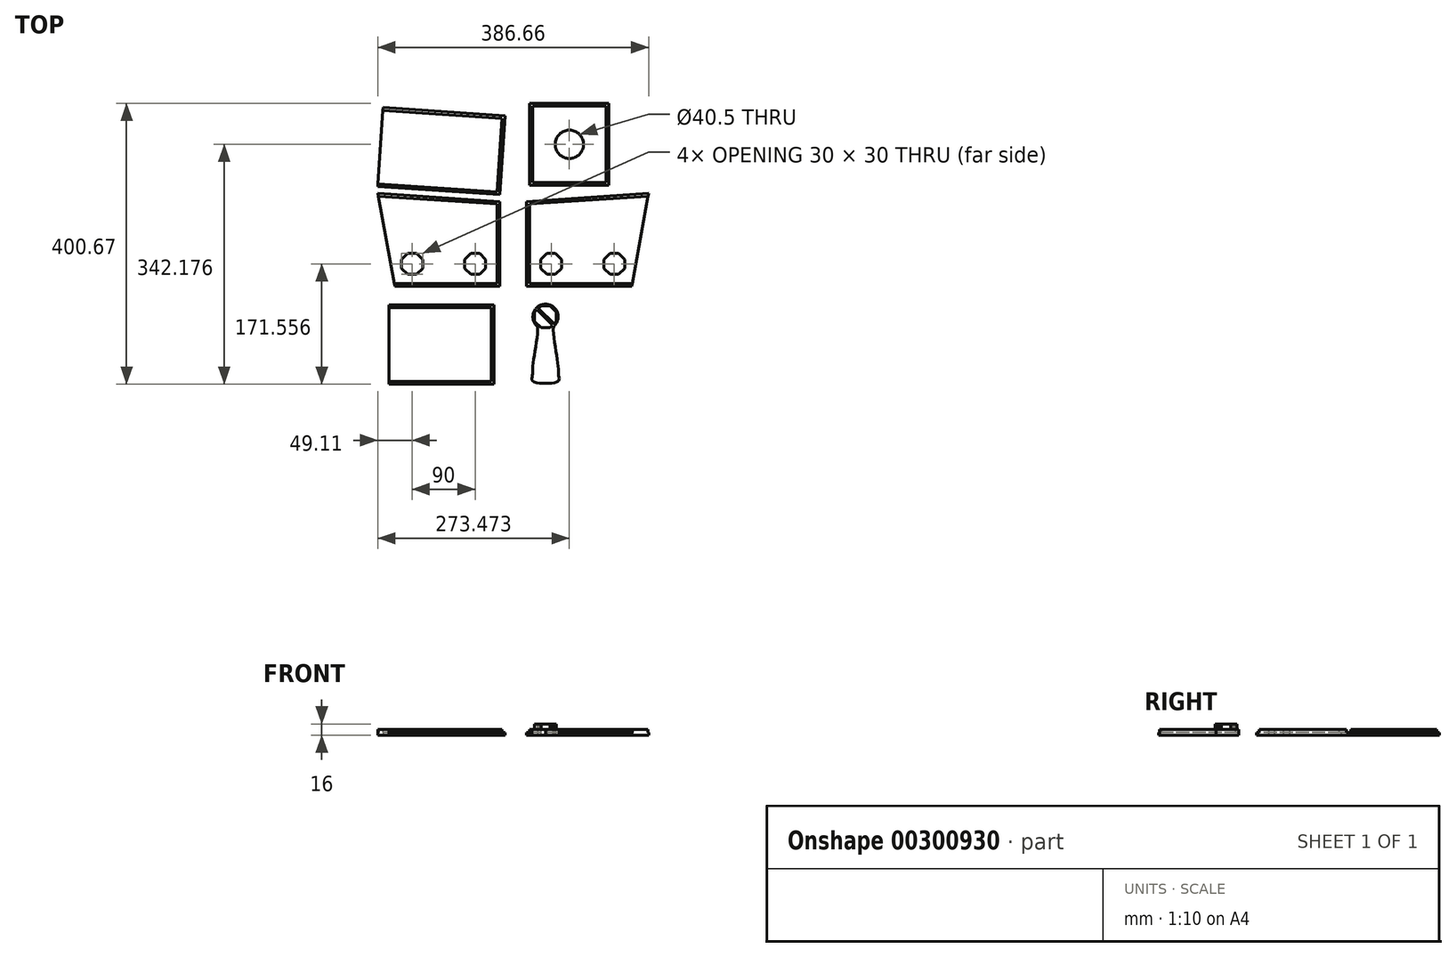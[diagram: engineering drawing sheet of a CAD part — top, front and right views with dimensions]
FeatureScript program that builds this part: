
annotation { "Feature Type Name" : "Feature", "Feature Type Description" : "" }
export const myFeature = defineFeature(function(context is Context, id is Id, definition is map)
    precondition{}
    {
        {
            assignVariable(context, id + "F0", {"name" : "mthick", "anyValue" : 8});
        }
        {
            var Q0;
            Q0=qCreatedBy(makeId("Top.planeOp"),FACE);
            var sketch = newSketch(context, id + "F1", { "sketchPlane" : qUnion([Q0])});
            skLineSegment(sketch, "E0", {"start": v(-19.22, -95.95) * mm, "end": v(-169.22, -95.95) * mm});
            skLineSegment(sketch, "E1", {"start": v(-169.22, -95.95) * mm, "end": v(-193.33, 36.65) * mm});
            skLineSegment(sketch, "E2", {"start": v(-193.33, 36.65) * mm, "end": v(-19.22, 25.05) * mm});
            skLineSegment(sketch, "E3", {"start": v(-19.22, 25.05) * mm, "end": v(-19.22, -95.95) * mm});
            skLineSegment(sketch, "E4", {"start": v(-169.22, -95.95) * mm, "end": v(-169.22, 35.05) * mm, "construction": true});
            skLineSegment(sketch, "E5", {"start": v(-19.22, 25.05) * mm, "end": v(-191.22, 25.05) * mm, "construction": true});
            skLineSegment(sketch, "E6", {"start": v(-60.43, -78.95) * mm, "end": v(-48, -78.95) * mm});
            skLineSegment(sketch, "E7", {"start": v(-48, -78.95) * mm, "end": v(-39.22, -70.17) * mm});
            skLineSegment(sketch, "E8", {"start": v(-39.22, -70.17) * mm, "end": v(-39.22, -57.74) * mm});
            skLineSegment(sketch, "E9", {"start": v(-39.22, -57.74) * mm, "end": v(-48, -48.95) * mm});
            skLineSegment(sketch, "E10", {"start": v(-48, -48.95) * mm, "end": v(-60.43, -48.95) * mm});
            skLineSegment(sketch, "E11", {"start": v(-60.43, -48.95) * mm, "end": v(-69.22, -57.74) * mm});
            skLineSegment(sketch, "E12", {"start": v(-69.22, -57.74) * mm, "end": v(-69.22, -70.17) * mm});
            skLineSegment(sketch, "E13", {"start": v(-69.22, -70.17) * mm, "end": v(-60.43, -78.95) * mm});
            skLineSegment(sketch, "E14", {"start": v(-60.43, -78.95) * mm, "end": v(-60.43, -48.95) * mm, "construction": true});
            skLineSegment(sketch, "E15", {"start": v(-69.22, -57.74) * mm, "end": v(-39.22, -57.74) * mm, "construction": true});
            skLineSegment(sketch, "E16.1.0.0", {"start": v(-129.22, -57.74) * mm, "end": v(-138, -48.95) * mm});
            skLineSegment(sketch, "E16.1.0.1", {"start": v(-150.43, -78.95) * mm, "end": v(-138, -78.95) * mm});
            skLineSegment(sketch, "E16.1.0.2", {"start": v(-138, -78.95) * mm, "end": v(-129.22, -70.17) * mm});
            skLineSegment(sketch, "E16.1.0.3", {"start": v(-159.22, -57.74) * mm, "end": v(-129.22, -57.74) * mm, "construction": true});
            skLineSegment(sketch, "E16.1.0.4", {"start": v(-159.22, -57.74) * mm, "end": v(-159.22, -70.17) * mm});
            skLineSegment(sketch, "E16.1.0.5", {"start": v(-150.43, -78.95) * mm, "end": v(-150.43, -48.95) * mm, "construction": true});
            skLineSegment(sketch, "E16.1.0.6", {"start": v(-150.43, -48.95) * mm, "end": v(-159.22, -57.74) * mm});
            skLineSegment(sketch, "E16.1.0.7", {"start": v(-138, -48.95) * mm, "end": v(-150.43, -48.95) * mm});
            skLineSegment(sketch, "E16.1.0.8", {"start": v(-129.22, -70.17) * mm, "end": v(-129.22, -57.74) * mm});
            skLineSegment(sketch, "E16.1.0.9", {"start": v(-159.22, -70.17) * mm, "end": v(-150.43, -78.95) * mm});
            skLineSegment(sketch, "E16.direction1", {"start": v(-69.22, -57.74) * mm, "end": v(-159.22, -57.74) * mm, "construction": true});
            skLineSegment(sketch, "E17.0", {"start": v(-23.22, -91.95) * mm, "end": v(-169.95, -91.95) * mm});
            skLineSegment(sketch, "E17.1", {"start": v(-23.22, 21.3) * mm, "end": v(-23.22, -91.95) * mm});
            skLineSegment(sketch, "E17.2", {"start": v(-192.6, 32.6) * mm, "end": v(-23.22, 21.3) * mm});
            skLineSegment(sketch, "E18.MirrorCS", {"start": v(60.43, -48.95) * mm, "end": v(69.22, -57.74) * mm});
            skLineSegment(sketch, "E19.MirrorCS", {"start": v(150.43, -48.95) * mm, "end": v(159.22, -57.74) * mm});
            skLineSegment(sketch, "E20.MirrorCS", {"start": v(69.22, -70.17) * mm, "end": v(60.43, -78.95) * mm});
            skLineSegment(sketch, "E21.MirrorCS", {"start": v(48, -48.95) * mm, "end": v(60.43, -48.95) * mm});
            skLineSegment(sketch, "E22.MirrorCS", {"start": v(138, -48.95) * mm, "end": v(150.43, -48.95) * mm});
            skLineSegment(sketch, "E23.MirrorCS", {"start": v(39.22, -57.74) * mm, "end": v(48, -48.95) * mm});
            skLineSegment(sketch, "E24.MirrorCS", {"start": v(129.22, -70.17) * mm, "end": v(129.22, -57.74) * mm});
            skLineSegment(sketch, "E25.MirrorCS", {"start": v(159.22, -57.74) * mm, "end": v(159.22, -70.17) * mm});
            skLineSegment(sketch, "E26.MirrorCS", {"start": v(129.22, -57.74) * mm, "end": v(138, -48.95) * mm});
            skLineSegment(sketch, "E27.MirrorCS", {"start": v(159.22, -70.17) * mm, "end": v(150.43, -78.95) * mm});
            skLineSegment(sketch, "E28.MirrorCS", {"start": v(69.22, -57.74) * mm, "end": v(69.22, -70.17) * mm});
            skLineSegment(sketch, "E29.MirrorCS", {"start": v(39.22, -70.17) * mm, "end": v(39.22, -57.74) * mm});
            skLineSegment(sketch, "E30.MirrorCS", {"start": v(150.43, -78.95) * mm, "end": v(138, -78.95) * mm});
            skLineSegment(sketch, "E31.MirrorCS", {"start": v(60.43, -78.95) * mm, "end": v(48, -78.95) * mm});
            skLineSegment(sketch, "E32.MirrorCS", {"start": v(138, -78.95) * mm, "end": v(129.22, -70.17) * mm});
            skLineSegment(sketch, "E33.MirrorCS", {"start": v(48, -78.95) * mm, "end": v(39.22, -70.17) * mm});
            skLineSegment(sketch, "E34.MirrorCS", {"start": v(150.43, -78.95) * mm, "end": v(150.43, -48.95) * mm, "construction": true});
            skLineSegment(sketch, "E35.MirrorCS", {"start": v(23.22, -91.95) * mm, "end": v(169.95, -91.95) * mm});
            skLineSegment(sketch, "E36.MirrorCS", {"start": v(192.6, 32.6) * mm, "end": v(23.22, 21.3) * mm});
            skLineSegment(sketch, "E37.MirrorCS", {"start": v(23.22, 21.3) * mm, "end": v(23.22, -91.95) * mm});
            skLineSegment(sketch, "E38.MirrorCS", {"start": v(169.22, -95.95) * mm, "end": v(193.33, 36.65) * mm});
            skLineSegment(sketch, "E39.MirrorCS", {"start": v(69.22, -57.74) * mm, "end": v(39.22, -57.74) * mm, "construction": true});
            skLineSegment(sketch, "E40.MirrorCS", {"start": v(19.22, -95.95) * mm, "end": v(169.22, -95.95) * mm});
            skLineSegment(sketch, "E41.MirrorCS", {"start": v(60.43, -78.95) * mm, "end": v(60.43, -48.95) * mm, "construction": true});
            skLineSegment(sketch, "E42.MirrorCS", {"start": v(193.33, 36.65) * mm, "end": v(19.22, 25.05) * mm});
            skLineSegment(sketch, "E43.MirrorCS", {"start": v(169.22, -95.95) * mm, "end": v(169.22, 35.05) * mm, "construction": true});
            skLineSegment(sketch, "E44.MirrorCS", {"start": v(19.22, 25.05) * mm, "end": v(191.22, 25.05) * mm, "construction": true});
            skLineSegment(sketch, "E45.MirrorCS", {"start": v(159.22, -57.74) * mm, "end": v(129.22, -57.74) * mm, "construction": true});
            skLineSegment(sketch, "E46.MirrorCS", {"start": v(69.22, -57.74) * mm, "end": v(159.22, -57.74) * mm, "construction": true});
            skLineSegment(sketch, "E47.MirrorCS", {"start": v(19.22, 25.05) * mm, "end": v(19.22, -95.95) * mm});
            skSolve(sketch);
        }
        {
            var Q0;
            Q0=qCreatedBy(makeId("Top.planeOp"),FACE);
            var sketch = newSketch(context, id + "F2", { "sketchPlane" : qUnion([Q0])});
            skLineSegment(sketch, "E48.bottom", {"start": v(-177.55, -122.5) * mm, "end": v(-27.55, -122.5) * mm});
            skLineSegment(sketch, "E48.top", {"start": v(-177.55, -235.5) * mm, "end": v(-27.55, -235.5) * mm});
            skLineSegment(sketch, "E48.left", {"start": v(-177.55, -122.5) * mm, "end": v(-177.55, -235.5) * mm});
            skLineSegment(sketch, "E48.right", {"start": v(-27.55, -122.5) * mm, "end": v(-27.55, -235.5) * mm});
            skLineSegment(sketch, "E49.0", {"start": v(-177.55, -231.5) * mm, "end": v(-31.55, -231.5) * mm});
            skLineSegment(sketch, "E49.1", {"start": v(-31.55, -126.5) * mm, "end": v(-31.55, -231.5) * mm});
            skLineSegment(sketch, "E49.2", {"start": v(-177.55, -126.5) * mm, "end": v(-31.55, -126.5) * mm});
            skSolve(sketch);
        }
        {
            var Q0;
            Q0=qCreatedBy(makeId("Top.planeOp"),FACE);
            var sketch = newSketch(context, id + "F3", { "sketchPlane" : qUnion([Q0])});
            skLineSegment(sketch, "E50.0", {"start": v(-193.33, 36.65) * mm, "end": v(-19.22, 25.05) * mm, "construction": true});
            skLineSegment(sketch, "E51", {"start": v(-193.33, 46.39) * mm, "end": v(-18.95, 34.76) * mm});
            skLineSegment(sketch, "E52", {"start": v(-18.95, 34.76) * mm, "end": v(-11.44, 147.51) * mm});
            skLineSegment(sketch, "E53", {"start": v(-11.44, 147.51) * mm, "end": v(-185.81, 159.14) * mm});
            skLineSegment(sketch, "E54", {"start": v(-185.81, 159.14) * mm, "end": v(-193.33, 46.39) * mm});
            skLineSegment(sketch, "E55.0", {"start": v(-15.7, 143.79) * mm, "end": v(-186.08, 155.15) * mm});
            skLineSegment(sketch, "E55.1", {"start": v(-22.68, 39.02) * mm, "end": v(-15.7, 143.79) * mm});
            skLineSegment(sketch, "E55.2", {"start": v(-193.06, 50.38) * mm, "end": v(-22.68, 39.02) * mm});
            skLineSegment(sketch, "E56.0", {"start": v(-192.6, 32.6) * mm, "end": v(-23.22, 21.3) * mm, "construction": true});
            skLineSegment(sketch, "E57.0", {"start": v(-19.22, 25.05) * mm, "end": v(-19.22, -95.95) * mm, "construction": true});
            skLineSegment(sketch, "E58", {"start": v(-23.22, 21.3) * mm, "end": v(-19.22, 21.04) * mm, "construction": true});
            skLineSegment(sketch, "E59", {"start": v(-19.22, 21.04) * mm, "end": v(-18.75, 28.14) * mm, "construction": true});
            skLineSegment(sketch, "E60", {"start": v(-19.22, 25.05) * mm, "end": v(-18.95, 25.03) * mm, "construction": true});
            skLineSegment(sketch, "E61", {"start": v(-193.33, 36.65) * mm, "end": v(-18.95, 25.03) * mm, "construction": true});
            skSolve(sketch);
        }
        {
            var Q0;
            Q0=qCreatedBy(makeId("Top.planeOp"),FACE);
            var sketch = newSketch(context, id + "F4", { "sketchPlane" : qUnion([Q0])});
            skPoint(sketch, "E62.0", {"position": v(-19.22, -95.95) * mm});
            skPoint(sketch, "E62.1", {"position": v(-19.22, 21.04) * mm});
            skLineSegment(sketch, "E63", {"start": v(-19.22, 21.04) * mm, "end": v(-19.22, -95.95) * mm, "construction": true});
            skLineSegment(sketch, "E64.bottom", {"start": v(136.64, 48.17) * mm, "end": v(23.64, 48.17) * mm});
            skLineSegment(sketch, "E64.top", {"start": v(136.64, 165.16) * mm, "end": v(23.64, 165.16) * mm});
            skLineSegment(sketch, "E64.left", {"start": v(136.64, 48.17) * mm, "end": v(136.64, 165.16) * mm});
            skLineSegment(sketch, "E64.right", {"start": v(23.64, 48.17) * mm, "end": v(23.64, 165.16) * mm});
            skPoint(sketch, "E64.middle", {"position": v(80.14, 106.67) * mm});
            skCircle(sketch, "E65", {"center": v(80.14, 106.67) * mm, "radius": 20.25 * mm});
            skLineSegment(sketch, "E66.0", {"start": v(132.64, 161.16) * mm, "end": v(27.64, 161.16) * mm});
            skLineSegment(sketch, "E66.1", {"start": v(132.64, 52.17) * mm, "end": v(132.64, 161.16) * mm});
            skLineSegment(sketch, "E66.2", {"start": v(132.64, 52.17) * mm, "end": v(27.64, 52.17) * mm});
            skLineSegment(sketch, "E66.3", {"start": v(27.64, 52.17) * mm, "end": v(27.64, 161.16) * mm});
            skSolve(sketch);
        }
        {
            var Q0;
            Q0=qCreatedBy(makeId("Top.planeOp"),FACE);
            var sketch = newSketch(context, id + "F5", { "sketchPlane" : qUnion([Q0])});
            skCircle(sketch, "E67", {"center": v(46.1, -139.4) * mm, "radius": 18 * mm});
            skLineSegment(sketch, "E68", {"start": v(46.1, -139.4) * mm, "end": v(46.1, -153.4) * mm, "construction": true});
            skLineSegment(sketch, "E69", {"start": v(46.1, -153.4) * mm, "end": v(34.78, -153.4) * mm, "construction": true});
            skLineSegment(sketch, "E70", {"start": v(46.1, -153.4) * mm, "end": v(57.4, -153.4) * mm, "construction": true});
            skLineSegment(sketch, "E71", {"start": v(46.1, -153.4) * mm, "end": v(46.1, -224.4) * mm, "construction": true});
            skLineSegment(sketch, "E72", {"start": v(46.1, -224.4) * mm, "end": v(27.1, -224.4) * mm, "construction": true});
            skLineSegment(sketch, "E73", {"start": v(46.1, -224.4) * mm, "end": v(46.1, -234.4) * mm, "construction": true});
            skFitSpline(sketch, "E74", {"points": [v(34.78, -153.4) * mm, v(28.54, -205.56) * mm, v(27.1, -224.4) * mm, v(27.1, -230.18) * mm, v(46.1, -234.4) * mm], "startDerivative": vector(7.27, -104.43) * mm, "endDerivative": vector(108.23, 10.07) * mm});
            skFitSpline(sketch, "E75.MirrorCS", {"points": [v(57.4, -153.4) * mm, v(63.64, -205.56) * mm, v(65.1, -224.4) * mm, v(65.1, -230.18) * mm, v(46.1, -234.4) * mm], "startDerivative": vector(-7.27, -104.43) * mm, "endDerivative": vector(-108.23, 10.07) * mm});
            skCircle(sketch, "E76.cCircle", {"center": v(46.1, -139.4) * mm, "radius": 15.5 * mm, "construction": true});
            skLineSegment(sketch, "E76.0", {"start": v(52.51, -123.9) * mm, "end": v(61.6, -132.98) * mm});
            skLineSegment(sketch, "E76.1", {"start": v(61.6, -132.98) * mm, "end": v(61.6, -145.82) * mm});
            skLineSegment(sketch, "E76.2", {"start": v(61.6, -145.82) * mm, "end": v(52.51, -154.9) * mm});
            skLineSegment(sketch, "E76.3", {"start": v(52.51, -154.9) * mm, "end": v(39.67, -154.9) * mm});
            skLineSegment(sketch, "E76.4", {"start": v(39.67, -154.9) * mm, "end": v(30.6, -145.82) * mm});
            skLineSegment(sketch, "E76.5", {"start": v(30.6, -145.82) * mm, "end": v(30.6, -132.98) * mm});
            skLineSegment(sketch, "E76.6", {"start": v(30.6, -132.98) * mm, "end": v(39.67, -123.9) * mm});
            skLineSegment(sketch, "E76.7", {"start": v(39.67, -123.9) * mm, "end": v(52.51, -123.9) * mm});
            skPoint(sketch, "E76.0.midPoint", {"position": v(57.05, -128.44) * mm});
            skLineSegment(sketch, "E77", {"start": v(35.13, -128.44) * mm, "end": v(57.05, -150.36) * mm, "construction": true});
            skLineSegment(sketch, "E78", {"start": v(34.07, -129.5) * mm, "end": v(55.99, -151.42) * mm});
            skLineSegment(sketch, "E79.MirrorCS", {"start": v(36.2, -127.38) * mm, "end": v(58.11, -149.3) * mm});
            skSolve(sketch);
        }
        {
            var Q0;
            Q0=makeQuery(id+"F1.imprint","IMPRINT",FACE,{"disambiguationData":[TD([[makeQuery(id+"F1.imprint","IMPRINT",EDGE,{"derivedFrom":sQuery(id+"F1.wireOp",EDGE,"E6")}),-1.0]])]});
            extrude(context, id + "F6", {"entities" : qUnion([Q0]), "depth" : (getVariable(context, 'mthick')) * mm});
        }
        {
            var Q0;
            {var subQ3=sQuery(id+"F1.wireOp",EDGE,"E0");Q0=makeQuery(id+"F1.imprint","IMPRINT",FACE,{"disambiguationData":[TD([[makeQuery(id+"F1.imprint","IMPRINT",EDGE,{"derivedFrom":subQ3}),-1.0]])]});}
            extrude(context, id + "F7", {"entities" : qUnion([Q0]), "operationType" : NewBodyOperationType.ADD, "depth" : (getVariable(context, 'mthick') / 2) * mm});
        }
        {
            var Q0;
            Q0=makeQuery(id+"F1.imprint","IMPRINT",FACE,{"disambiguationData":[TD([[makeQuery(id+"F1.imprint","IMPRINT",EDGE,{"derivedFrom":sQuery(id+"F1.wireOp",EDGE,"E18.MirrorCS")}),1.0]])]});
            extrude(context, id + "F8", {"entities" : qUnion([Q0]), "depth" : (getVariable(context, 'mthick')) * mm});
        }
        {
            var Q0;
            {var subQ1=sQuery(id+"F1.wireOp",EDGE,"E35.MirrorCS");Q0=makeQuery(id+"F1.imprint","IMPRINT",FACE,{"disambiguationData":[TD([[makeQuery(id+"F1.imprint","IMPRINT",EDGE,{"derivedFrom":subQ1}),-1.0]])]});}
            extrude(context, id + "F9", {"entities" : qUnion([Q0]), "operationType" : NewBodyOperationType.ADD, "depth" : (getVariable(context, 'mthick') / 2) * mm});
        }
        {
            var Q0;
            {var subQ0=sQuery(id+"F3.wireOp",EDGE,"E55.0");Q0=makeQuery(id+"F3.imprint","IMPRINT",FACE,{"disambiguationData":[TD([[makeQuery(id+"F3.imprint","IMPRINT",EDGE,{"derivedFrom":subQ0}),1.0]])]});}
            extrude(context, id + "F10", {"entities" : qUnion([Q0]), "depth" : (getVariable(context, 'mthick')) * mm});
        }
        {
            var Q0;
            {var subQ3=sQuery(id+"F3.wireOp",EDGE,"E51");Q0=makeQuery(id+"F3.imprint","IMPRINT",FACE,{"disambiguationData":[TD([[makeQuery(id+"F3.imprint","IMPRINT",EDGE,{"derivedFrom":subQ3}),1.0]])]});}
            extrude(context, id + "F11", {"entities" : qUnion([Q0]), "operationType" : NewBodyOperationType.ADD, "depth" : (getVariable(context, 'mthick') / 2) * mm});
        }
        {
            var Q0;
            {var subQ0=sQuery(id+"F2.wireOp",EDGE,"E49.0");Q0=makeQuery(id+"F2.imprint","IMPRINT",FACE,{"disambiguationData":[TD([[makeQuery(id+"F2.imprint","IMPRINT",EDGE,{"derivedFrom":subQ0}),1.0]])]});}
            extrude(context, id + "F12", {"entities" : qUnion([Q0]), "depth" : (getVariable(context, 'mthick')) * mm});
        }
        {
            var Q0;
            {var subQ3=sQuery(id+"F2.wireOp",EDGE,"E48.bottom");Q0=makeQuery(id+"F2.imprint","IMPRINT",FACE,{"disambiguationData":[TD([[makeQuery(id+"F2.imprint","IMPRINT",EDGE,{"derivedFrom":subQ3}),-1.0]])]});}
            extrude(context, id + "F13", {"entities" : qUnion([Q0]), "operationType" : NewBodyOperationType.ADD, "depth" : (getVariable(context, 'mthick') / 2) * mm});
        }
        {
            var Q0;
            Q0=makeQuery(id+"F4.imprint","IMPRINT",FACE,{"disambiguationData":[TD([[makeQuery(id+"F4.imprint","IMPRINT",EDGE,{"derivedFrom":sQuery(id+"F4.wireOp",EDGE,"E65")}),-1.0]])]});
            extrude(context, id + "F14", {"entities" : qUnion([Q0]), "depth" : (getVariable(context, 'mthick')) * mm});
        }
        {
            var Q0;
            Q0=makeQuery(id+"F4.imprint","IMPRINT",FACE,{"disambiguationData":[TD([[makeQuery(id+"F4.imprint","IMPRINT",EDGE,{"derivedFrom":sQuery(id+"F4.wireOp",EDGE,"E64.bottom")}),-1.0]])]});
            extrude(context, id + "F15", {"entities" : qUnion([Q0]), "operationType" : NewBodyOperationType.ADD, "depth" : (getVariable(context, 'mthick') / 2) * mm});
        }
        {
            var Q0;
            {var subQ1=sQuery(id+"F5.wireOp",EDGE,"E76.3");Q0=makeQuery(id+"F5.imprint","IMPRINT",FACE,{"disambiguationData":[TD([[makeQuery(id+"F5.imprint","IMPRINT",EDGE,{"derivedFrom":subQ1}),-1.0]])]});}
            var Q1;
            Q1=makeQuery(id+"F5.imprint","IMPRINT",FACE,{"disambiguationData":[TD([[makeQuery(id+"F5.imprint","IMPRINT",EDGE,{"derivedFrom":sQuery(id+"F5.wireOp",EDGE,"E76.0")}),-1.0]])]});
            extrude(context, id + "F16", {"entities" : qUnion([Q0, Q1]), "depth" : (getVariable(context, 'mthick') * 2) * mm});
        }
        {
            var Q0;
            {var subQ0=sQuery(id+"F5.wireOp",EDGE,"E74");Q0=makeQuery(id+"F5.imprint","IMPRINT",FACE,{"disambiguationData":[TD([[makeQuery(id+"F5.imprint","IMPRINT",EDGE,{"derivedFrom":subQ0}),1.0]])]});}
            var Q1;
            Q1=makeQuery(id+"F5.imprint","IMPRINT",FACE,{"disambiguationData":[TD([[makeQuery(id+"F5.imprint","IMPRINT",EDGE,{"derivedFrom":sQuery(id+"F5.wireOp",EDGE,"E76.0")}),1.0]])]});
            var Q2;
            {var subQ0=sQuery(id+"F5.wireOp",EDGE,"E78");Q2=makeQuery(id+"F5.imprint","IMPRINT",FACE,{"disambiguationData":[TD([[makeQuery(id+"F5.imprint","IMPRINT",EDGE,{"derivedFrom":subQ0}),1.0]])]});}
            extrude(context, id + "F17", {"entities" : qUnion([Q0, Q1, Q2]), "operationType" : NewBodyOperationType.ADD, "depth" : (getVariable(context, 'mthick')) * mm});
        }
    });
